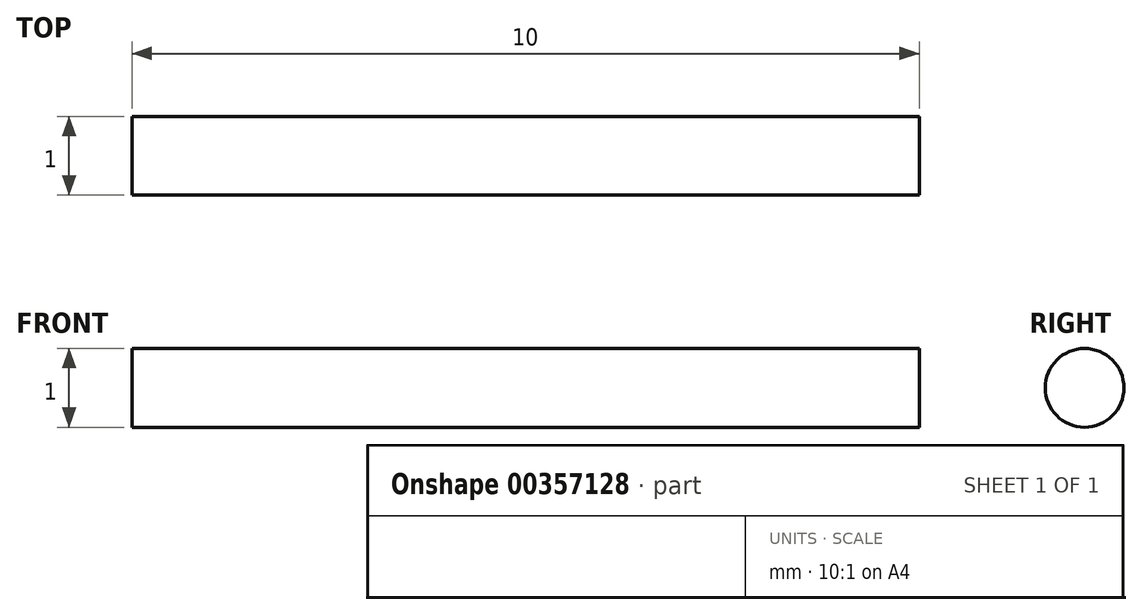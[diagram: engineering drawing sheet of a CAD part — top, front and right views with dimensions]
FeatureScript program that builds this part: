
annotation { "Feature Type Name" : "Feature", "Feature Type Description" : "" }
export const myFeature = defineFeature(function(context is Context, id is Id, definition is map)
    precondition{}
    {
        {
            var Q0;
            Q0=qCreatedBy(makeId("Right.planeOp"),FACE);
            var sketch = newSketch(context, id + "F0", { "sketchPlane" : qUnion([Q0])});
            skCircle(sketch, "E0", {"center": v(0, 0) * mm, "radius": 0.5 * mm});
            skSolve(sketch);
        }
        {
            var Q0;
            Q0=makeQuery(id+"F0.imprint","IMPRINT",FACE,{"disambiguationData":[TD([[makeQuery(id+"F0.imprint","IMPRINT",EDGE,{"derivedFrom":sQuery(id+"F0.wireOp",EDGE,"E0")}),1.0]])]});
            extrude(context, id + "F1", {"entities" : qUnion([Q0]), "depth" : 10 * mm});
        }
    });
